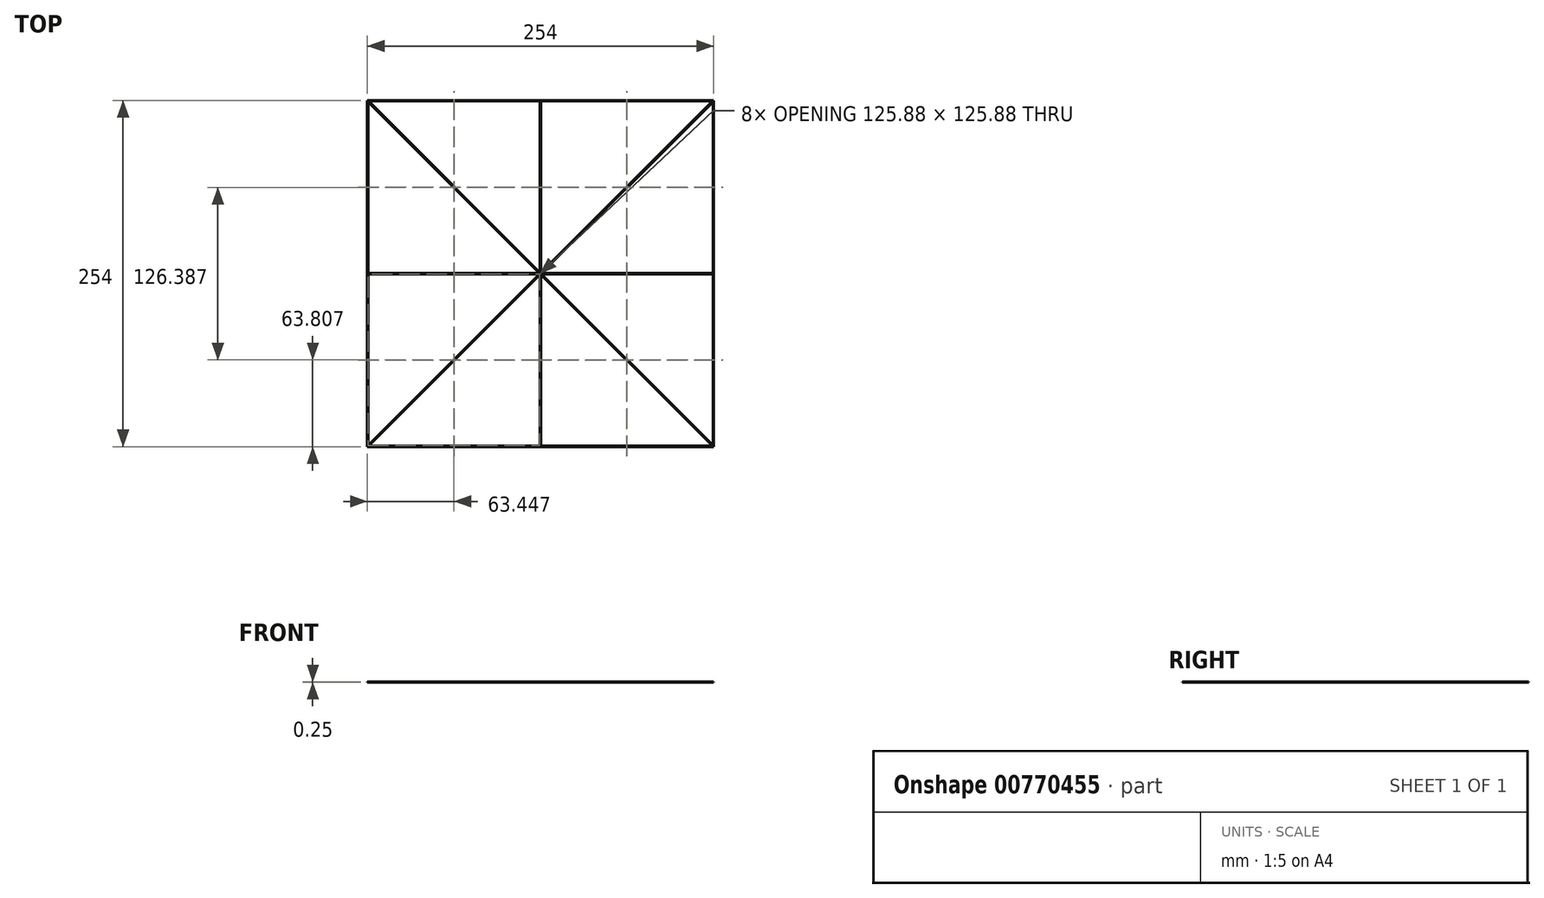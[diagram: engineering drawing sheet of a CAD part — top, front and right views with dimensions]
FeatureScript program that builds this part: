
annotation { "Feature Type Name" : "Feature", "Feature Type Description" : "" }
export const myFeature = defineFeature(function(context is Context, id is Id, definition is map)
    precondition{}
    {
        {
            var Q0;
            Q0=qCreatedBy(makeId("Top.planeOp"),FACE);
            var sketch = newSketch(context, id + "F0", { "sketchPlane" : qUnion([Q0])});
            skLineSegment(sketch, "E0.bottom", {"start": v(-127, -127) * mm, "end": v(127, -127) * mm, "construction": true});
            skLineSegment(sketch, "E0.top", {"start": v(-127, 127) * mm, "end": v(127, 127) * mm, "construction": true});
            skLineSegment(sketch, "E0.left", {"start": v(-127, -127) * mm, "end": v(-127, 127) * mm, "construction": true});
            skLineSegment(sketch, "E0.right", {"start": v(127, -127) * mm, "end": v(127, 127) * mm, "construction": true});
            skPoint(sketch, "E0.middle", {"position": v(0, 0) * mm});
            skLineSegment(sketch, "E1.bottom", {"start": v(-126.5, -126.5) * mm, "end": v(126.5, -126.5) * mm, "construction": true});
            skLineSegment(sketch, "E1.top", {"start": v(-126.5, 126.5) * mm, "end": v(126.5, 126.5) * mm, "construction": true});
            skLineSegment(sketch, "E1.left", {"start": v(-126.5, -126.5) * mm, "end": v(-126.5, 126.5) * mm, "construction": true});
            skLineSegment(sketch, "E1.right", {"start": v(126.5, -126.5) * mm, "end": v(126.5, 126.5) * mm, "construction": true});
            skLineSegment(sketch, "E2", {"start": v(0, 0) * mm, "end": v(0, 126.5) * mm, "construction": true});
            skLineSegment(sketch, "E3", {"start": v(-126.5, 126.5) * mm, "end": v(126.5, -126.5) * mm, "construction": true});
            skLineSegment(sketch, "E4", {"start": v(-126.5, -126.5) * mm, "end": v(126.5, 126.5) * mm, "construction": true});
            skLineSegment(sketch, "E5", {"start": v(0, 0) * mm, "end": v(-126.5, 0) * mm, "construction": true});
            skLineSegment(sketch, "E6", {"start": v(-0.25, 126.5) * mm, "end": v(-0.25, -126.5) * mm, "construction": true});
            skLineSegment(sketch, "E7", {"start": v(0.25, 126.5) * mm, "end": v(0.25, -126.5) * mm, "construction": true});
            skLineSegment(sketch, "E8", {"start": v(126.13, 126.5) * mm, "end": v(-126.5, -126.13) * mm, "construction": true});
            skLineSegment(sketch, "E9.0", {"start": v(126.5, 126.13) * mm, "end": v(-126.13, -126.5) * mm, "construction": true});
            skLineSegment(sketch, "E10.0", {"start": v(-126.5, 126.13) * mm, "end": v(126.13, -126.5) * mm, "construction": true});
            skLineSegment(sketch, "E11.0", {"start": v(-126.13, 126.5) * mm, "end": v(126.5, -126.13) * mm, "construction": true});
            skLineSegment(sketch, "E12.0", {"start": v(126.5, 0.25) * mm, "end": v(-126.5, 0.25) * mm, "construction": true});
            skLineSegment(sketch, "E13.0", {"start": v(126.5, -0.25) * mm, "end": v(-126.5, -0.25) * mm, "construction": true});
            skSolve(sketch);
        }
        {
            var Q0;
            Q0=qCreatedBy(makeId("Top.planeOp"),FACE);
            var sketch = newSketch(context, id + "F1", { "sketchPlane" : qUnion([Q0])});
            skPoint(sketch, "E14.middle", {"position": v(0, 0) * mm});
            skLineSegment(sketch, "E15.0", {"start": v(-127, 127) * mm, "end": v(127, 127) * mm});
            skLineSegment(sketch, "E16.1", {"start": v(127, -127) * mm, "end": v(127, 127) * mm});
            skLineSegment(sketch, "E17.1", {"start": v(-127, -127) * mm, "end": v(127, -127) * mm});
            skLineSegment(sketch, "E18.0", {"start": v(-127, -127) * mm, "end": v(-127, 127) * mm});
            skLineSegment(sketch, "E19.0", {"start": v(-126.13, 126.5) * mm, "end": v(-0.25, 126.5) * mm});
            skLineSegment(sketch, "E20.0", {"start": v(-0.25, 126.5) * mm, "end": v(-0.25, 0.61) * mm});
            skLineSegment(sketch, "E21.0", {"start": v(0.25, 126.5) * mm, "end": v(0.25, 0.61) * mm});
            skLineSegment(sketch, "E22.0", {"start": v(-126.5, -126.13) * mm, "end": v(-126.5, -0.25) * mm});
            skLineSegment(sketch, "E23.0", {"start": v(-126.13, 126.5) * mm, "end": v(-0.25, 0.61) * mm});
            skLineSegment(sketch, "E24.0", {"start": v(-126.5, 126.13) * mm, "end": v(-0.61, 0.25) * mm});
            skLineSegment(sketch, "E25.0", {"start": v(126.5, -126.13) * mm, "end": v(126.5, -0.25) * mm});
            skLineSegment(sketch, "E26.0", {"start": v(-126.13, -126.5) * mm, "end": v(-0.25, -126.5) * mm});
            skLineSegment(sketch, "E27.0", {"start": v(126.5, 126.13) * mm, "end": v(0.61, 0.25) * mm});
            skLineSegment(sketch, "E28.0", {"start": v(126.13, 126.5) * mm, "end": v(0.25, 0.61) * mm});
            skLineSegment(sketch, "E29.0", {"start": v(126.5, 0.25) * mm, "end": v(0.61, 0.25) * mm});
            skLineSegment(sketch, "E30.0", {"start": v(126.5, -0.25) * mm, "end": v(0.61, -0.25) * mm});
            skLineSegment(sketch, "E31.trimOffspring", {"start": v(0.25, 126.5) * mm, "end": v(126.13, 126.5) * mm});
            skLineSegment(sketch, "E32.trimOffspring", {"start": v(0.25, -126.5) * mm, "end": v(126.13, -126.5) * mm});
            skLineSegment(sketch, "E33.trimOffspring", {"start": v(126.5, 0.25) * mm, "end": v(126.5, 126.13) * mm});
            skLineSegment(sketch, "E34.trimOffspring", {"start": v(-126.5, 0.25) * mm, "end": v(-126.5, 126.13) * mm});
            skLineSegment(sketch, "E35.trimOffspring", {"start": v(-0.61, 0.25) * mm, "end": v(-126.5, 0.25) * mm});
            skLineSegment(sketch, "E36.trimOffspring", {"start": v(0.61, -0.25) * mm, "end": v(126.5, -126.13) * mm});
            skLineSegment(sketch, "E37.trimOffspring", {"start": v(0.25, -0.61) * mm, "end": v(0.25, -126.5) * mm});
            skLineSegment(sketch, "E38.trimOffspring", {"start": v(0.25, -0.61) * mm, "end": v(126.13, -126.5) * mm});
            skLineSegment(sketch, "E39.trimOffspring", {"start": v(-0.25, -0.61) * mm, "end": v(-126.13, -126.5) * mm});
            skLineSegment(sketch, "E40.trimOffspring", {"start": v(-0.61, -0.25) * mm, "end": v(-126.5, -126.13) * mm});
            skLineSegment(sketch, "E41.trimOffspring", {"start": v(-0.61, -0.25) * mm, "end": v(-126.5, -0.25) * mm});
            skLineSegment(sketch, "E42.trimOffspring", {"start": v(-0.25, -0.61) * mm, "end": v(-0.25, -126.5) * mm});
            skPoint(sketch, "E43.orphan", {"position": v(-126.5, 126.5) * mm});
            skPoint(sketch, "E44.orphan", {"position": v(126.5, 126.5) * mm});
            skPoint(sketch, "E45.orphan", {"position": v(126.5, -126.5) * mm});
            skPoint(sketch, "E46.orphan", {"position": v(-126.5, -126.5) * mm});
            skSolve(sketch);
        }
        {
            var Q0;
            Q0=qSketchRegion(id+"F1",true);
            extrude(context, id + "F2", {"entities" : qUnion([Q0]), "depth" : 0.25 * mm, "offsetDistance" : 25.4 * mm});
        }
    });
